# Revit family: IS_Mara_A9042_BIM_IT
name_source: partatom
category: Plumbing Fixtures
revit_build: Autodesk Revit 2015 (Build: 20140606_1530(x64)
units: mm (PartAtom-declared; Revit-internal decimal feet)

## types (1)
- A9042AA - MARA MISC.LAVABO INC A MURO KIT2 ORIZ.
    Accesso = www.idealstandard.it
    Accessori = www.idealstandard.it
    AltezzaNominale = 0
    BIMobject category = Basins
    BOSUseNativeGeometries = 1
    Brand = Ideal Standard
    Brand url = www.idealstandard.it
    Caratteristiche = Miscelatore monocomando lavabo per installazione a parete. È dotato di bocca di erogazione fissa e aeratore M16,5x1 con portata massima di 5 l/min. Cartuccia da 47 mm con riduttore di temperatura. Il miscelatore lavora con il corpo incasso A5948NU da ordinare separatamente. Solo parti a vista.
    CodiceABarre = 4015413327817
    Colore = Cromato
    Connessione = Installazione
    CostoDiSostituzione = 0 $
    Description = MARA - Miscelatore monocomando lavabo per installazione a parete. È dotato di bocca di erogazione fissa e aeratore M16,5x1 con portata massima di 5 l/min. Cartuccia da 47 mm con riduttore di temperatura. Il miscelatore lavora con il corpo incasso A5948NU da ordinare separatamente. Solo parti a vista.
    DurataGaranzia = 5
    DurataGaranziaProdotti = 5
    EAN code = https://4015413327817
    Edition number = 1
    Finitura = Cromato
    Forma = Sculptura
    Garanzia = Garanzia Idealstandard
    IFC Classification = Valve
    InformaziniGaranzia = www.idealstandard.it/garanzia.html
    InformazioniGaranzia = www.idealstandard.it/garanzia.html
    Installation instructions = http://www.idealspec.co.uk
    InstruzioniInstallazione = www.idealstandard.it/garanzia.html
    LarghezzaNominale = 0
    LunghezzaNominale = 0
    Manufacturer name = Ideal Standard
    Material main = Ottone
    Materiale = Ottone
    Model = A9042AA
    NBS Reference Code = 75-70-52-96
    NBS Reference Description = Water Supply Systems Control Systems
    Nome = MARA MISC.LAVABO INC A MURO KIT2 ORIZ.
    Nominal height = 114
    Nominal width = 193
    NumeroDiModello = A9042AA
    OmniClass Code = 23.45.55.17
    OmniClass Description = SanitaryTerminal
    PesoNetto = 1,3 KG
    Product Guid = 8a4a16be-0ab3-4dbb-8538-b12f11cf9459
    Product SKU = A9042
    Product data url = https://bimobject.com
    Product family = Sanitary
    Product group = Washbasin taps
    Product name = MARA MISC.LAVABO INC A MURO KIT2 ORIZ.
    Product url = https://bimobject.com
    ProfonditaNominale = 0
    QR code = http://bimobject.com
    Spazio = Interno
    Technical description = MARA MISC.LAVABO INC A MURO KIT2 ORIZ.
    Telefono = 800 652 290
    TipoDiDato = Fisso
    URL = www.idealstandard.it
    Uniclass 2.0 Code = SS-75-70-52-96
    Uniclass 2.0 Description = Water Supply Systems Control Systems
    Uniclass 2015 Code = Pr_40_20_87_96
    Uniclass 2015 Name = Washbasin manual water supply sets
    UnitaDurata = anni
    UnitaDurataGaranzia = anni
    UnitaLineare = millimetri
    UnitaVolume = Litri
    Versione = 1
    Weight Net (Kg) = 1.3

## geometry (parser evidence)
native form markers: Blend x4, Sweep x1
no freeform markers — native parametric forms only
